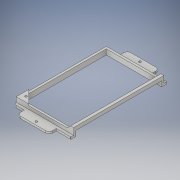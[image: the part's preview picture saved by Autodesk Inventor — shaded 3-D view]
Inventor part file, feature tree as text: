
AUTODESK INVENTOR PART (.ipt)
format: ipt  version: 2019 (Build 230136000, 136)  size: 250,368 bytes
history: native  units: mm
features: extrude x9, sketch x8, projected_geometry x8, plane x2, other x1, hole x1
ambient origin geometry x8: Origin, YZ Plane, XZ Plane, XY Plane, X Axis, Y Axis, Z Axis, Center Point
bodies: Volumenkörper1 (feature_tree)
feature tree (29):
  extrude  "Extrusion1"  Depth=121.0mm
  sketch  "Skizze2"  dims[d2=3.0mm d3=7.5mm d4=0.0mm]
  extrude  "Extrusion2"  Depth=7.5mm TaperAngle=0.0deg
  extrude  "Extrusion3"  Depth=4.5mm
  other  "Arbeitsachse1"
  sketch  "Skizze4"  dims[d7=18.0mm d9=18.0mm]
  extrude  "Extrusion4"  Depth=18.0mm
  extrude  "Extrusion5"  Depth=3.0mm
  hole  "Bohrung1"  [1 undecoded]
  extrude  "Extrusion8"  Depth=4.0mm
  extrude  "Extrusion9"  Depth=4.0mm
  extrude  "Extrusion10"  Depth=4.0mm
  extrude  "Extrusion11"  Depth=4.0mm
  sketch  "Skizze1"  dims[d0=78.0mm d1=121.0mm]
  sketch  "Skizze3"  dims[d5=4.5mm d6=3.5mm]
  plane  "Arbeitsebene1"
  plane  "Arbeitsebene2"
  projected_geometry  "Projizierte Kontur1"
  sketch  "Skizze6"  dims[d10=2.0mm d11=0.0mm d12=3.0mm]
  projected_geometry  "Projizierte Kontur3"
  projected_geometry  "Projizierte Kontur4"
  projected_geometry  "Projizierte Kontur5"
  sketch  "Skizze7"  dims[d13=3.0mm d14=0.0mm d20=155.0mm]
  projected_geometry  "Projizierte Kontur6"
  projected_geometry  "Projizierte Kontur7"
  sketch  "Skizze8"  dims[d21=45.0mm d22=4.0mm]
  projected_geometry  "Projizierte Kontur8"
  sketch  "Skizze9"  dims[d23=135.0mm d24=4.0mm d25=4.0mm d26=4.0mm d27=4.0mm d28=3.0mm d29=0.0mm d30=5.0mm d31=3.0mm d32=0.0mm d33=5.5mm d34=3.0mm d35=6.0mm d36=4.0mm d37=2.0mm d38=90.0deg d39=10.0mm d40=0.0mm d46=10.0mm d47=0.0mm d48=4.0mm d49=5.0mm d50=0.0mm d51=45.0deg d52=5.0mm d53=0.0mm d54=5.0mm d55=0.0mm]
  projected_geometry  "Projizierte Kontur9"
note: 1 required parameter value undecoded (feature->parameter linkage not recoverable at this tier; creation-order binding heuristic only, values carry confidence <= 0.55)
